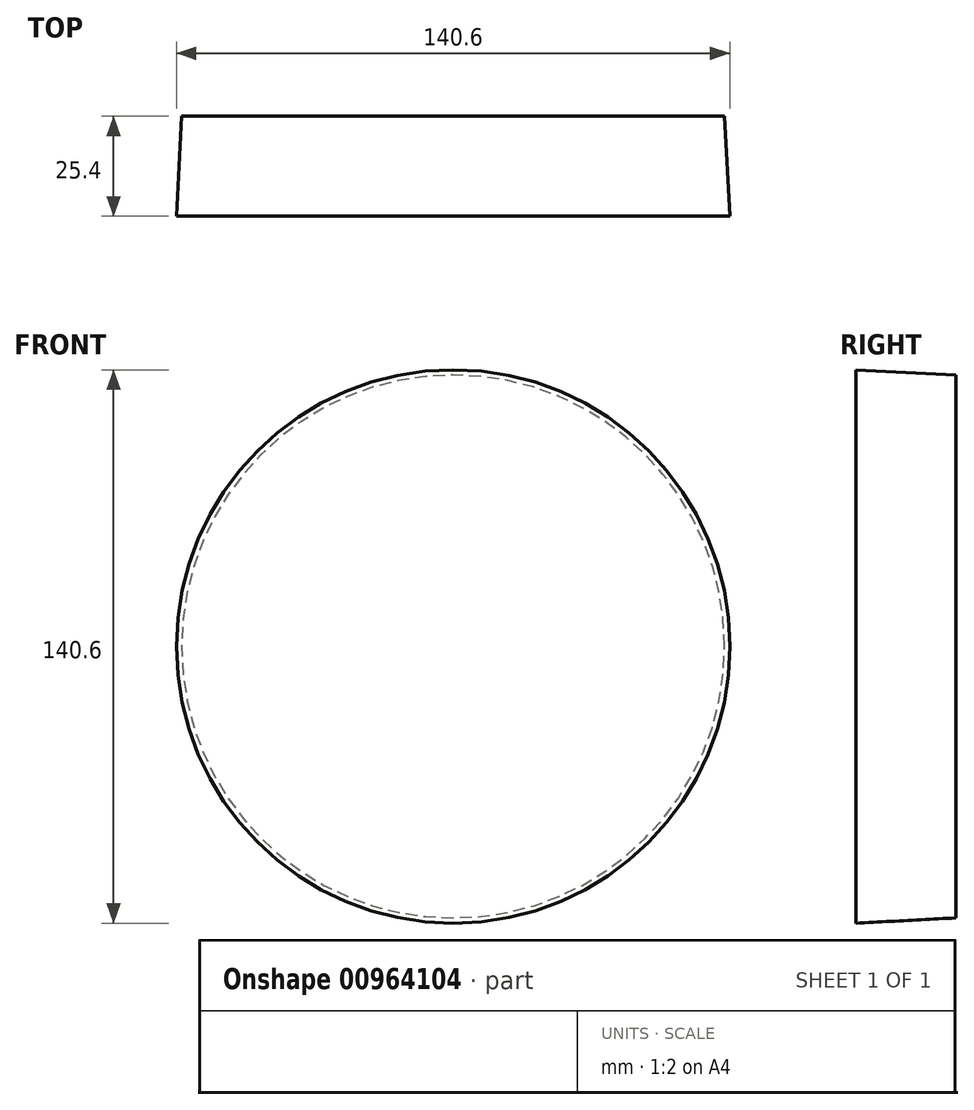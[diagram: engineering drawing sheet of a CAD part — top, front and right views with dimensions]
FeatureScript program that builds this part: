
annotation { "Feature Type Name" : "Feature", "Feature Type Description" : "" }
export const myFeature = defineFeature(function(context is Context, id is Id, definition is map)
    precondition{}
    {
        {
            var Q0;
            Q0=qCreatedBy(makeId("Front.planeOp"),FACE);
            var sketch = newSketch(context, id + "F0", { "sketchPlane" : qUnion([Q0])});
            skCircle(sketch, "E0", {"center": v(0, 0) * mm, "radius": 68.97 * mm});
            skSolve(sketch);
        }
        {
            var Q0;
            Q0 = qSketchRegion(id + "F0", true);
            extrude(context, id + "F1", {"entities" : qUnion([Q0]), "depth" : 25.4 * mm, "offsetDistance" : 25.4 * mm, "hasDraft" : true, "draftAngle" : 3 * degree});
        }
    });
